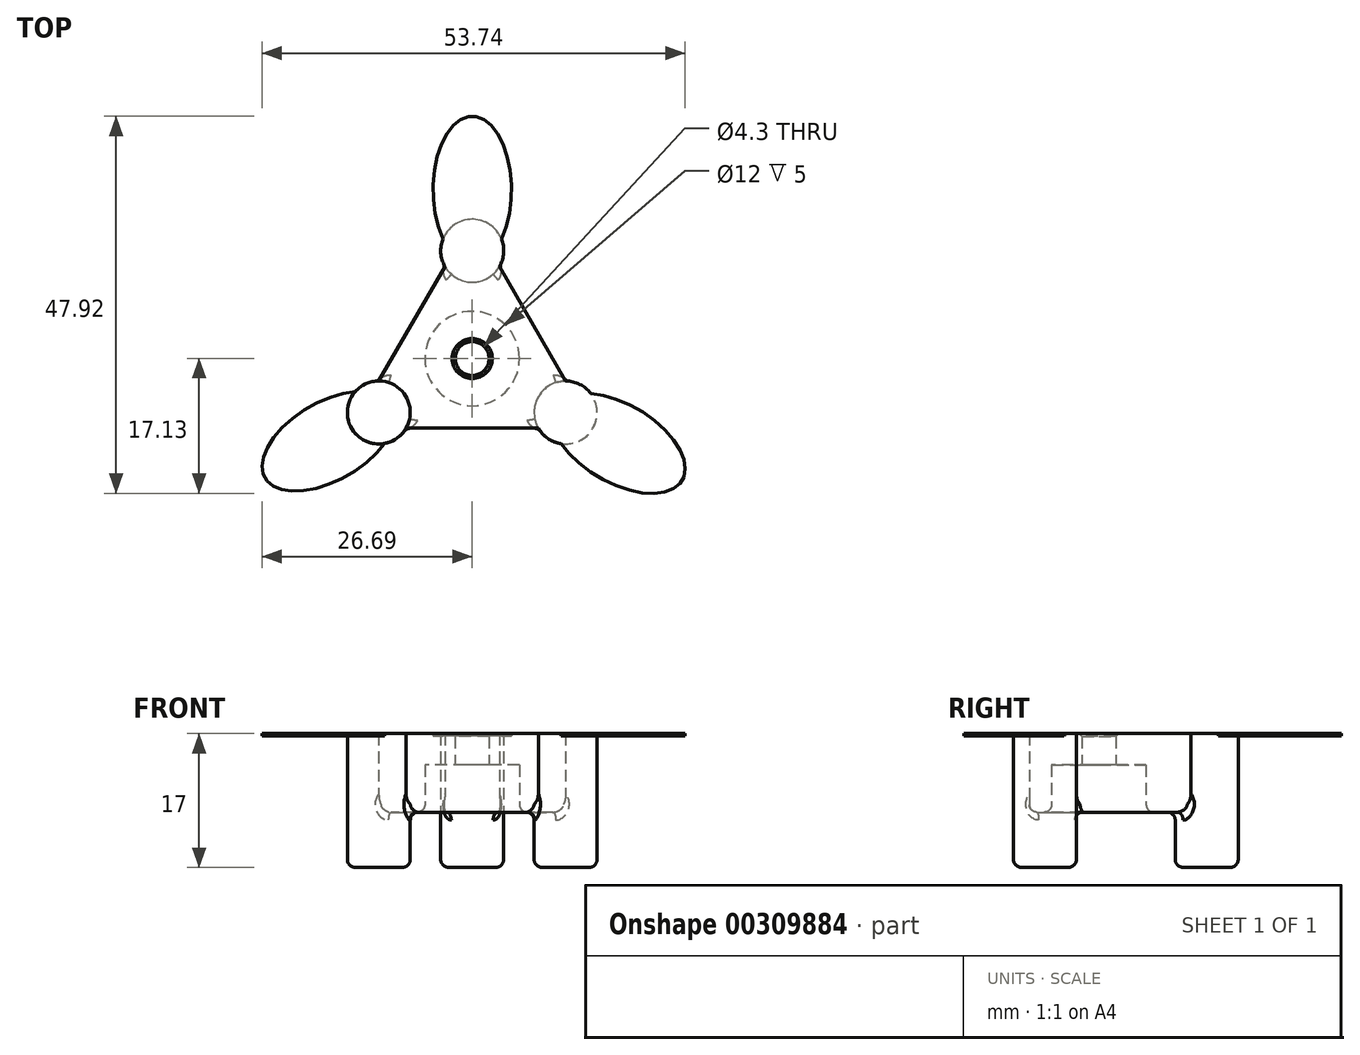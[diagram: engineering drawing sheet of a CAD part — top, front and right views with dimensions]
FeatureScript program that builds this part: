
annotation { "Feature Type Name" : "Feature", "Feature Type Description" : "" }
export const myFeature = defineFeature(function(context is Context, id is Id, definition is map)
    precondition{}
    {
        {
            var Q0;
            Q0=qCreatedBy(makeId("Top.planeOp"),FACE);
            var sketch = newSketch(context, id + "F0", { "sketchPlane" : qUnion([Q0])});
            skArc(sketch, "E0.cCircle", {"start": v(-20, -6.3) * mm, "mid": v(-22, -6.45) * mm, "end": v(-23.96, -6.88) * mm, "construction": true});
            skLineSegment(sketch, "E0.0", {"start": v(-28.4, -28.85) * mm, "end": v(-31.86, -26.85) * mm});
            skLineSegment(sketch, "E0.1", {"start": v(-31.86, -26.85) * mm, "end": v(-31.86, -22.85) * mm});
            skLineSegment(sketch, "E0.2", {"start": v(-23.46, -8.3) * mm, "end": v(-20, -6.3) * mm});
            skLineSegment(sketch, "E0.3", {"start": v(-20, -6.3) * mm, "end": v(-16.54, -8.3) * mm});
            skLineSegment(sketch, "E0.4", {"start": v(-8.14, -22.85) * mm, "end": v(-8.14, -26.85) * mm});
            skLineSegment(sketch, "E0.5", {"start": v(-8.14, -26.85) * mm, "end": v(-11.6, -28.85) * mm});
            skCircle(sketch, "E1", {"center": v(-20, -6.3) * mm, "radius": 4 * mm});
            skCircle(sketch, "E2", {"center": v(-8.14, -26.85) * mm, "radius": 4 * mm});
            skCircle(sketch, "E3", {"center": v(-31.86, -26.85) * mm, "radius": 4 * mm});
            skCircle(sketch, "E4", {"center": v(-20, -20) * mm, "radius": 2.15 * mm});
            skCircle(sketch, "E5", {"center": v(-20, -20) * mm, "radius": 6 * mm});
            skPoint(sketch, "E6.orphan", {"position": v(-8.14, -13.15) * mm});
            skPoint(sketch, "E7.0.midPoint", {"position": v(-20, -13.4) * mm});
            skPoint(sketch, "E8.0.midPoint", {"position": v(-20, -11.5) * mm});
            skLineSegment(sketch, "E9", {"start": v(-16.54, -8.3) * mm, "end": v(-8.14, -22.85) * mm});
            skLineSegment(sketch, "E10", {"start": v(-11.6, -28.85) * mm, "end": v(-28.4, -28.85) * mm});
            skLineSegment(sketch, "E11", {"start": v(-31.86, -22.85) * mm, "end": v(-23.46, -8.3) * mm});
            skPoint(sketch, "E12.orphan", {"position": v(-23.81, -13.4) * mm});
            skPoint(sketch, "E7.1.start.orphan", {"position": v(-16.19, -13.4) * mm});
            skPoint(sketch, "E13.orphan", {"position": v(-15.1, -11.5) * mm});
            skPoint(sketch, "E14.orphan", {"position": v(-10.19, -20) * mm});
            skPoint(sketch, "E15.orphan", {"position": v(-29.81, -20) * mm});
            skPoint(sketch, "E8.5.end.orphan", {"position": v(-24.9, -11.5) * mm});
            skSolve(sketch);
        }
        {
            var Q0;
            Q0=makeQuery(id+"F0.imprint","IMPRINT",FACE,{"disambiguationData":[TD([[makeQuery(id+"F0.imprint","IMPRINT",EDGE,{"derivedFrom":sQuery(id+"F0.wireOp",EDGE,"E7.0")}),1.0]])]});
            var Q1;
            Q1=makeQuery(id+"F0.imprint","IMPRINT",FACE,{"disambiguationData":[TD([[makeQuery(id+"F0.imprint","IMPRINT",EDGE,{"derivedFrom":sQuery(id+"F0.wireOp",EDGE,"E4")}),-1.0]])]});
            var Q2;
            Q2=makeQuery(id+"F0.imprint","IMPRINT",FACE,{"disambiguationData":[TD([[makeQuery(id+"F0.imprint","IMPRINT",EDGE,{"derivedFrom":sQuery(id+"F0.wireOp",EDGE,"E5")}),-1.0]])]});
            var Q3;
            {var subQ0=sQuery(id+"F0.wireOp",EDGE,"E0.2");Q3=makeQuery(id+"F0.imprint","IMPRINT",FACE,{"disambiguationData":[TD([[makeQuery(id+"F0.imprint","IMPRINT",EDGE,{"derivedFrom":subQ0}),-1.0]])]});}
            var Q4;
            {var subQ0=sQuery(id+"F0.wireOp",EDGE,"E0.2");Q4=makeQuery(id+"F0.imprint","IMPRINT",FACE,{"disambiguationData":[TD([[makeQuery(id+"F0.imprint","IMPRINT",EDGE,{"derivedFrom":subQ0}),1.0]])]});}
            var Q5;
            Q5=makeQuery(id+"F0.imprint","IMPRINT",FACE,{"disambiguationData":[TD([[makeQuery(id+"F0.imprint","IMPRINT",EDGE,{"derivedFrom":sQuery(id+"F0.wireOp",EDGE,"E8.0")}),1.0]])]});
            var Q6;
            {var subQ0=sQuery(id+"F0.wireOp",EDGE,"E0.0");Q6=makeQuery(id+"F0.imprint","IMPRINT",FACE,{"disambiguationData":[TD([[makeQuery(id+"F0.imprint","IMPRINT",EDGE,{"derivedFrom":subQ0}),1.0]])]});}
            var Q7;
            {var subQ0=sQuery(id+"F0.wireOp",EDGE,"E0.4");Q7=makeQuery(id+"F0.imprint","IMPRINT",FACE,{"disambiguationData":[TD([[makeQuery(id+"F0.imprint","IMPRINT",EDGE,{"derivedFrom":subQ0}),1.0]])]});}
            var Q8;
            {var subQ0=sQuery(id+"F0.wireOp",EDGE,"E0.4");Q8=makeQuery(id+"F0.imprint","IMPRINT",FACE,{"disambiguationData":[TD([[makeQuery(id+"F0.imprint","IMPRINT",EDGE,{"derivedFrom":subQ0}),-1.0]])]});}
            var Q9;
            {var subQ0=sQuery(id+"F0.wireOp",EDGE,"E0.0");Q9=makeQuery(id+"F0.imprint","IMPRINT",FACE,{"disambiguationData":[TD([[makeQuery(id+"F0.imprint","IMPRINT",EDGE,{"derivedFrom":subQ0}),-1.0]])]});}
            extrude(context, id + "F1", {"entities" : qUnion([Q0, Q1, Q2, Q3, Q4, Q5, Q6, Q7, Q8, Q9]), "depth" : 10 * mm});
        }
        {
            var Q0;
            Q0=makeQuery(id+"F0.imprint","IMPRINT",FACE,{"disambiguationData":[TD([[makeQuery(id+"F0.imprint","IMPRINT",EDGE,{"derivedFrom":sQuery(id+"F0.wireOp",EDGE,"E8.0")}),1.0]])]});
            var Q1;
            {var subQ0=sQuery(id+"F0.wireOp",EDGE,"E0.2");Q1=makeQuery(id+"F0.imprint","IMPRINT",FACE,{"disambiguationData":[TD([[makeQuery(id+"F0.imprint","IMPRINT",EDGE,{"derivedFrom":subQ0}),-1.0]])]});}
            var Q2;
            {var subQ0=sQuery(id+"F0.wireOp",EDGE,"E0.2");Q2=makeQuery(id+"F0.imprint","IMPRINT",FACE,{"disambiguationData":[TD([[makeQuery(id+"F0.imprint","IMPRINT",EDGE,{"derivedFrom":subQ0}),1.0]])]});}
            var Q3;
            {var subQ0=sQuery(id+"F0.wireOp",EDGE,"E0.0");Q3=makeQuery(id+"F0.imprint","IMPRINT",FACE,{"disambiguationData":[TD([[makeQuery(id+"F0.imprint","IMPRINT",EDGE,{"derivedFrom":subQ0}),-1.0]])]});}
            var Q4;
            {var subQ0=sQuery(id+"F0.wireOp",EDGE,"E0.0");Q4=makeQuery(id+"F0.imprint","IMPRINT",FACE,{"disambiguationData":[TD([[makeQuery(id+"F0.imprint","IMPRINT",EDGE,{"derivedFrom":subQ0}),1.0]])]});}
            var Q5;
            {var subQ0=sQuery(id+"F0.wireOp",EDGE,"E0.4");Q5=makeQuery(id+"F0.imprint","IMPRINT",FACE,{"disambiguationData":[TD([[makeQuery(id+"F0.imprint","IMPRINT",EDGE,{"derivedFrom":subQ0}),-1.0]])]});}
            var Q6;
            {var subQ0=sQuery(id+"F0.wireOp",EDGE,"E0.4");Q6=makeQuery(id+"F0.imprint","IMPRINT",FACE,{"disambiguationData":[TD([[makeQuery(id+"F0.imprint","IMPRINT",EDGE,{"derivedFrom":subQ0}),1.0]])]});}
            extrude(context, id + "F2", {"entities" : qUnion([Q0, Q1, Q2, Q3, Q4, Q5, Q6]), "operationType" : NewBodyOperationType.ADD, "depth" : 2.5 * mm});
        }
        {
            var Q0;
            Q0=makeQuery(id+"F0.imprint","IMPRINT",FACE,{"disambiguationData":[TD([[makeQuery(id+"F0.imprint","IMPRINT",EDGE,{"derivedFrom":sQuery(id+"F0.wireOp",EDGE,"E4")}),-1.0]])]});
            var Q1;
            Q1=makeQuery(id+"F0.imprint","IMPRINT",FACE,{"disambiguationData":[TD([[makeQuery(id+"F0.imprint","IMPRINT",EDGE,{"derivedFrom":sQuery(id+"F0.wireOp",EDGE,"E5")}),-1.0]])]});
            extrude(context, id + "F3", {"entities" : qUnion([Q0, Q1]), "operationType" : NewBodyOperationType.REMOVE, "depth" : 6 * mm});
        }
        {
            var Q0;
            {var subQ0=sQuery(id+"F0.wireOp",EDGE,"E0.4");Q0=makeQuery(id+"F0.imprint","IMPRINT",FACE,{"disambiguationData":[TD([[makeQuery(id+"F0.imprint","IMPRINT",EDGE,{"derivedFrom":subQ0}),-1.0]])]});}
            var Q1;
            {var subQ0=sQuery(id+"F0.wireOp",EDGE,"E0.2");Q1=makeQuery(id+"F0.imprint","IMPRINT",FACE,{"disambiguationData":[TD([[makeQuery(id+"F0.imprint","IMPRINT",EDGE,{"derivedFrom":subQ0}),-1.0]])]});}
            var Q2;
            {var subQ0=sQuery(id+"F0.wireOp",EDGE,"E0.2");Q2=makeQuery(id+"F0.imprint","IMPRINT",FACE,{"disambiguationData":[TD([[makeQuery(id+"F0.imprint","IMPRINT",EDGE,{"derivedFrom":subQ0}),1.0]])]});}
            var Q3;
            {var subQ0=sQuery(id+"F0.wireOp",EDGE,"E0.0");Q3=makeQuery(id+"F0.imprint","IMPRINT",FACE,{"disambiguationData":[TD([[makeQuery(id+"F0.imprint","IMPRINT",EDGE,{"derivedFrom":subQ0}),-1.0]])]});}
            var Q4;
            {var subQ0=sQuery(id+"F0.wireOp",EDGE,"E0.0");Q4=makeQuery(id+"F0.imprint","IMPRINT",FACE,{"disambiguationData":[TD([[makeQuery(id+"F0.imprint","IMPRINT",EDGE,{"derivedFrom":subQ0}),1.0]])]});}
            var Q5;
            {var subQ0=sQuery(id+"F0.wireOp",EDGE,"E0.4");Q5=makeQuery(id+"F0.imprint","IMPRINT",FACE,{"disambiguationData":[TD([[makeQuery(id+"F0.imprint","IMPRINT",EDGE,{"derivedFrom":subQ0}),1.0]])]});}
            extrude(context, id + "F4", {"entities" : qUnion([Q0, Q1, Q2, Q3, Q4, Q5]), "operationType" : NewBodyOperationType.ADD, "oppositeDirection" : true, "depth" : 7 * mm});
        }
        {
            var Q0;
            Q0=makeQuery(id+"F1.opExtrude","CAP_FACE",FACE,{"disambiguationData":[OSD([sQuery(id+"F0.wireOp",EDGE,"E1"),sQuery(id+"F0.wireOp",EDGE,"E2"),sQuery(id+"F0.wireOp",EDGE,"E3"),sQuery(id+"F0.wireOp",EDGE,"E4"),sQuery(id+"F0.wireOp",EDGE,"E9"),sQuery(id+"F0.wireOp",EDGE,"E10"),sQuery(id+"F0.wireOp",EDGE,"E11")])],"isStart":false});
            var sketch = newSketch(context, id + "F5", { "sketchPlane" : qUnion([Q0])});
            skEllipse(sketch, "E16", {"center": v(-20, 1.45) * mm, "majorRadius": 9.34 * mm, "minorRadius": 4.98 * mm, "majorAxis": v(0, -1)});
            skEllipse(sketch, "E17", {"center": v(-1.41, -30.78) * mm, "majorRadius": 9.34 * mm, "minorRadius": 4.98 * mm, "majorAxis": v(-0.87, 0.5)});
            skEllipse(sketch, "E18", {"center": v(-38.23, -30.48) * mm, "majorRadius": 9.34 * mm, "minorRadius": 4.98 * mm, "majorAxis": v(-0.87, -0.5)});
            skSolve(sketch);
        }
        {
            var Q0;
            {var subQ0=sQuery(id+"F5.wireOp",EDGE,"E16");var subQ1=sQuery(id+"F0.wireOp",EDGE,"E1");var subQ2=makeQuery(id+"FhOCBRzYYn4Nzte_2.opFillet","BLEND_EDGE",EDGE,{"blendedFrom":[makeQuery(id+"F1.opExtrude","CAP_EDGE",EDGE,{"disambiguationData":[OSD([subQ1])],"isStart":false}),makeQuery(id+"F1.opExtrude","CAP_FACE",FACE,{"disambiguationData":[OSD([subQ1,sQuery(id+"F0.wireOp",EDGE,"E2"),sQuery(id+"F0.wireOp",EDGE,"E3"),sQuery(id+"F0.wireOp",EDGE,"E4"),sQuery(id+"F0.wireOp",EDGE,"E9"),sQuery(id+"F0.wireOp",EDGE,"E10"),sQuery(id+"F0.wireOp",EDGE,"E11")])],"isStart":false})],"blendedInto":[makeQuery(id+"F1.opExtrude","CAP_FACE",FACE,{"disambiguationData":[OSD([subQ1,sQuery(id+"F0.wireOp",EDGE,"E2"),sQuery(id+"F0.wireOp",EDGE,"E3"),sQuery(id+"F0.wireOp",EDGE,"E4"),sQuery(id+"F0.wireOp",EDGE,"E9"),sQuery(id+"F0.wireOp",EDGE,"E10"),sQuery(id+"F0.wireOp",EDGE,"E11")])],"isStart":false})]});var subQ3=makeQuery(id+"F5.imprint","INTERSECT",VERTEX,{"disambiguationData":[OD(0.0)],"derivedFrom":[subQ2,subQ0]});Q0=makeQuery(id+"F5.imprint","IMPRINT",FACE,{"disambiguationData":[TD([[makeQuery(id+"F5.imprint","IMPRINT",EDGE,{"disambiguationData":[TD([[subQ3,1.0]])],"derivedFrom":subQ0}),1.0]])]});}
            var Q1;
            {var subQ0=sQuery(id+"F5.wireOp",EDGE,"E18");var subQ1=sQuery(id+"F0.wireOp",EDGE,"E3");var subQ2=makeQuery(id+"FhOCBRzYYn4Nzte_2.opFillet","BLEND_EDGE",EDGE,{"blendedFrom":[makeQuery(id+"F1.opExtrude","CAP_EDGE",EDGE,{"disambiguationData":[OSD([subQ1])],"isStart":false}),makeQuery(id+"F1.opExtrude","CAP_FACE",FACE,{"disambiguationData":[OSD([sQuery(id+"F0.wireOp",EDGE,"E1"),sQuery(id+"F0.wireOp",EDGE,"E2"),subQ1,sQuery(id+"F0.wireOp",EDGE,"E4"),sQuery(id+"F0.wireOp",EDGE,"E9"),sQuery(id+"F0.wireOp",EDGE,"E10"),sQuery(id+"F0.wireOp",EDGE,"E11")])],"isStart":false})],"blendedInto":[makeQuery(id+"F1.opExtrude","CAP_FACE",FACE,{"disambiguationData":[OSD([sQuery(id+"F0.wireOp",EDGE,"E1"),sQuery(id+"F0.wireOp",EDGE,"E2"),subQ1,sQuery(id+"F0.wireOp",EDGE,"E4"),sQuery(id+"F0.wireOp",EDGE,"E9"),sQuery(id+"F0.wireOp",EDGE,"E10"),sQuery(id+"F0.wireOp",EDGE,"E11")])],"isStart":false})]});var subQ3=makeQuery(id+"F5.imprint","INTERSECT",VERTEX,{"disambiguationData":[OD(0.0)],"derivedFrom":[subQ2,subQ0]});Q1=makeQuery(id+"F5.imprint","IMPRINT",FACE,{"disambiguationData":[TD([[makeQuery(id+"F5.imprint","IMPRINT",EDGE,{"disambiguationData":[TD([[subQ3,1.0]])],"derivedFrom":subQ0}),1.0]])]});}
            var Q2;
            {var subQ0=sQuery(id+"F5.wireOp",EDGE,"E17");var subQ1=sQuery(id+"F0.wireOp",EDGE,"E2");var subQ2=makeQuery(id+"FhOCBRzYYn4Nzte_2.opFillet","BLEND_EDGE",EDGE,{"blendedFrom":[makeQuery(id+"F1.opExtrude","CAP_EDGE",EDGE,{"disambiguationData":[OSD([subQ1])],"isStart":false}),makeQuery(id+"F1.opExtrude","CAP_FACE",FACE,{"disambiguationData":[OSD([sQuery(id+"F0.wireOp",EDGE,"E1"),subQ1,sQuery(id+"F0.wireOp",EDGE,"E3"),sQuery(id+"F0.wireOp",EDGE,"E4"),sQuery(id+"F0.wireOp",EDGE,"E9"),sQuery(id+"F0.wireOp",EDGE,"E10"),sQuery(id+"F0.wireOp",EDGE,"E11")])],"isStart":false})],"blendedInto":[makeQuery(id+"F1.opExtrude","CAP_FACE",FACE,{"disambiguationData":[OSD([sQuery(id+"F0.wireOp",EDGE,"E1"),subQ1,sQuery(id+"F0.wireOp",EDGE,"E3"),sQuery(id+"F0.wireOp",EDGE,"E4"),sQuery(id+"F0.wireOp",EDGE,"E9"),sQuery(id+"F0.wireOp",EDGE,"E10"),sQuery(id+"F0.wireOp",EDGE,"E11")])],"isStart":false})]});var subQ3=makeQuery(id+"F5.imprint","INTERSECT",VERTEX,{"disambiguationData":[OD(0.0)],"derivedFrom":[subQ2,subQ0]});Q2=makeQuery(id+"F5.imprint","IMPRINT",FACE,{"disambiguationData":[TD([[makeQuery(id+"F5.imprint","IMPRINT",EDGE,{"disambiguationData":[TD([[subQ3,1.0]])],"derivedFrom":subQ0}),1.0]])]});}
            extrude(context, id + "F6", {"entities" : qUnion([Q0, Q1, Q2]), "operationType" : NewBodyOperationType.ADD, "oppositeDirection" : true, "depth" : 0.3 * mm});
        }
        {
            var Q0;
            Q0=makeQuery(id+"F3.boolean.opBoolean","COPY",FACE,{"derivedFrom":makeQuery(id+"F3.opExtrude","CAP_FACE",FACE,{"disambiguationData":[OSD([sQuery(id+"F0.wireOp",EDGE,"E1"),sQuery(id+"F0.wireOp",EDGE,"E2"),sQuery(id+"F0.wireOp",EDGE,"E3"),sQuery(id+"F0.wireOp",EDGE,"E4"),sQuery(id+"F0.wireOp",EDGE,"E9"),sQuery(id+"F0.wireOp",EDGE,"E10"),sQuery(id+"F0.wireOp",EDGE,"E11")])],"isStart":false})});
            extrude(context, id + "F7", {"entities" : qUnion([Q0]), "operationType" : NewBodyOperationType.ADD, "depth" : 6 * mm});
        }
        {
            var Q0;
            Q0=makeQuery(id+"F0.imprint","IMPRINT",FACE,{"disambiguationData":[TD([[makeQuery(id+"F0.imprint","IMPRINT",EDGE,{"derivedFrom":sQuery(id+"F0.wireOp",EDGE,"E4")}),-1.0]])]});
            extrude(context, id + "F8", {"entities" : qUnion([Q0]), "operationType" : NewBodyOperationType.REMOVE, "depth" : 6 * mm});
        }
        {
            var Q0;
            Q0=makeQuery(id+"F7.opExtrude","CAP_FACE",FACE,{"disambiguationData":[OSD([sQuery(id+"F0.wireOp",EDGE,"E1"),sQuery(id+"F0.wireOp",EDGE,"E2"),sQuery(id+"F0.wireOp",EDGE,"E3"),sQuery(id+"F0.wireOp",EDGE,"E4"),sQuery(id+"F0.wireOp",EDGE,"E9"),sQuery(id+"F0.wireOp",EDGE,"E10"),sQuery(id+"F0.wireOp",EDGE,"E11")])],"isStart":false});
            var Q1;
            Q1=makeQuery(id+"F4.opExtrude","CAP_FACE",FACE,{"disambiguationData":[OSD([sQuery(id+"F0.wireOp",EDGE,"E2")])],"isStart":false});
            var Q2;
            Q2=makeQuery(id+"F4.opExtrude","CAP_FACE",FACE,{"disambiguationData":[OSD([sQuery(id+"F0.wireOp",EDGE,"E1")])],"isStart":false});
            var Q3;
            Q3=makeQuery(id+"F4.opExtrude","CAP_FACE",FACE,{"disambiguationData":[OSD([sQuery(id+"F0.wireOp",EDGE,"E3")])],"isStart":false});
            fillet(context, id + "F9", {"entities" : qUnion([Q0, Q1, Q2, Q3]), "radius" : 1 * mm, "tangentPropagation" : true, "allowEdgeOverflow" : false});
        }
        {
            var Q0;
            Q0=makeQuery(id+"F8.boolean.opBoolean","COPY",EDGE,{"derivedFrom":makeQuery(id+"F8.opExtrude","CAP_EDGE",EDGE,{"disambiguationData":[OSD([sQuery(id+"F0.wireOp",EDGE,"E4")])],"isStart":false})});
            var Q1;
            Q1=makeQuery(id+"F1.opExtrude","CAP_EDGE",EDGE,{"disambiguationData":[OSD([sQuery(id+"F0.wireOp",EDGE,"E4")])],"isStart":false});
            chamfer(context, id + "F10", {"entities" : qUnion([Q0, Q1]), "width" : 0.4 * mm, "tangentPropagation" : true});
        }
    });
